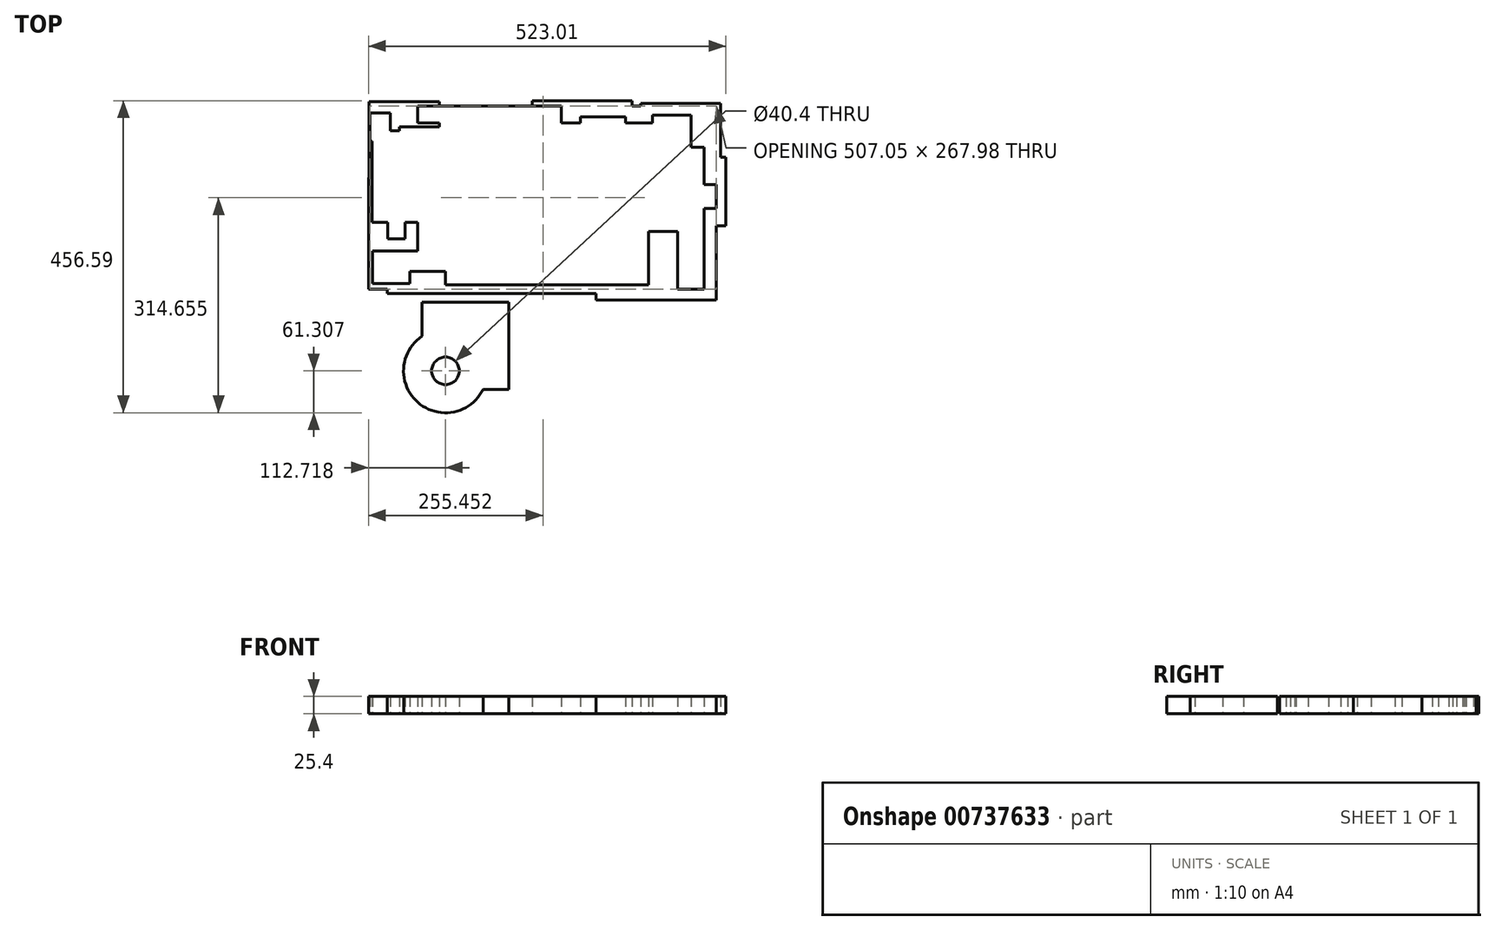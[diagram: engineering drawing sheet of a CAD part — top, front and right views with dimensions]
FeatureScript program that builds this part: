
annotation { "Feature Type Name" : "Feature", "Feature Type Description" : "" }
export const myFeature = defineFeature(function(context is Context, id is Id, definition is map)
    precondition{}
    {
        {
            var Q0;
            Q0=qCreatedBy(makeId("Top.planeOp"),FACE);
            var sketch = newSketch(context, id + "F0", { "sketchPlane" : qUnion([Q0])});
            skLineSegment(sketch, "E0.bottom", {"start": v(-153.8, 86.38) * mm, "end": v(142.89, 86.38) * mm});
            skLineSegment(sketch, "E0.top", {"start": v(-153.8, -120.85) * mm, "end": v(142.89, -120.85) * mm});
            skLineSegment(sketch, "E0.left", {"start": v(-153.8, 86.38) * mm, "end": v(-153.8, -120.85) * mm});
            skLineSegment(sketch, "E0.right", {"start": v(142.89, 86.38) * mm, "end": v(142.89, -120.85) * mm});
            skLineSegment(sketch, "E1.bottom", {"start": v(-264.86, 130.4) * mm, "end": v(-234.77, 130.4) * mm});
            skLineSegment(sketch, "E1.top", {"start": v(-264.86, 89.63) * mm, "end": v(-234.77, 89.63) * mm});
            skLineSegment(sketch, "E1.left", {"start": v(-264.86, 130.4) * mm, "end": v(-264.86, 89.63) * mm});
            skLineSegment(sketch, "E1.right", {"start": v(-234.77, 130.4) * mm, "end": v(-234.77, 89.63) * mm});
            skLineSegment(sketch, "E2.bottom", {"start": v(-229.05, 51.8) * mm, "end": v(-195.45, 51.8) * mm});
            skLineSegment(sketch, "E2.top", {"start": v(-229.05, 13.14) * mm, "end": v(-195.45, 13.14) * mm});
            skLineSegment(sketch, "E2.left", {"start": v(-229.05, 51.8) * mm, "end": v(-229.05, 13.14) * mm});
            skLineSegment(sketch, "E2.right", {"start": v(-195.45, 51.8) * mm, "end": v(-195.45, 13.14) * mm});
            skLineSegment(sketch, "E3.bottom", {"start": v(-238.55, -17.95) * mm, "end": v(-212.9, -17.95) * mm});
            skLineSegment(sketch, "E3.top", {"start": v(-238.55, -53.72) * mm, "end": v(-212.9, -53.72) * mm});
            skLineSegment(sketch, "E3.left", {"start": v(-238.55, -17.95) * mm, "end": v(-238.55, -53.72) * mm});
            skLineSegment(sketch, "E3.right", {"start": v(-212.9, -17.95) * mm, "end": v(-212.9, -53.72) * mm});
            skLineSegment(sketch, "E4.bottom", {"start": v(-261.02, -70.92) * mm, "end": v(-206.29, -70.92) * mm});
            skLineSegment(sketch, "E4.top", {"start": v(-261.02, -118.62) * mm, "end": v(-206.29, -118.62) * mm});
            skLineSegment(sketch, "E4.left", {"start": v(-261.02, -70.92) * mm, "end": v(-261.02, -118.62) * mm});
            skLineSegment(sketch, "E4.right", {"start": v(-206.29, -70.92) * mm, "end": v(-206.29, -118.62) * mm});
            skLineSegment(sketch, "E5.bottom", {"start": v(-194.84, 140.76) * mm, "end": v(224.73, 140.76) * mm});
            skLineSegment(sketch, "E5.top", {"start": v(-194.84, 116.08) * mm, "end": v(224.73, 116.08) * mm});
            skLineSegment(sketch, "E5.left", {"start": v(-194.84, 140.76) * mm, "end": v(-194.84, 116.08) * mm});
            skLineSegment(sketch, "E5.right", {"start": v(224.73, 140.76) * mm, "end": v(224.73, 116.08) * mm});
            skLineSegment(sketch, "E6.bottom", {"start": v(185.58, 80.44) * mm, "end": v(224.07, 80.44) * mm});
            skLineSegment(sketch, "E6.top", {"start": v(185.58, -127.21) * mm, "end": v(224.07, -127.21) * mm});
            skLineSegment(sketch, "E6.left", {"start": v(185.58, 80.44) * mm, "end": v(185.58, -127.21) * mm});
            skLineSegment(sketch, "E6.right", {"start": v(224.07, 80.44) * mm, "end": v(224.07, -127.21) * mm});
            skLineSegment(sketch, "E7.bottom", {"start": v(118.03, 26.13) * mm, "end": v(242.19, 26.13) * mm});
            skLineSegment(sketch, "E7.top", {"start": v(118.03, -8.97) * mm, "end": v(242.19, -8.97) * mm});
            skLineSegment(sketch, "E7.left", {"start": v(118.03, 26.13) * mm, "end": v(118.03, -8.97) * mm});
            skLineSegment(sketch, "E7.right", {"start": v(242.19, 26.13) * mm, "end": v(242.19, -8.97) * mm});
            skLineSegment(sketch, "E8.bottom", {"start": v(-261.46, 140.94) * mm, "end": v(15.43, 140.94) * mm});
            skLineSegment(sketch, "E8.top", {"start": v(-261.46, -29.37) * mm, "end": v(15.43, -29.37) * mm});
            skLineSegment(sketch, "E8.left", {"start": v(-261.46, 140.94) * mm, "end": v(-261.46, -29.37) * mm});
            skLineSegment(sketch, "E8.right", {"start": v(15.43, 140.94) * mm, "end": v(15.43, -29.37) * mm});
            skLineSegment(sketch, "E9.bottom", {"start": v(-194.87, 0) * mm, "end": v(-43.2, 0) * mm});
            skLineSegment(sketch, "E9.top", {"start": v(-194.87, -101.23) * mm, "end": v(-43.2, -101.23) * mm});
            skLineSegment(sketch, "E9.left", {"start": v(-194.87, 0) * mm, "end": v(-194.87, -101.23) * mm});
            skLineSegment(sketch, "E9.right", {"start": v(-43.2, 0) * mm, "end": v(-43.2, -101.23) * mm});
            skLineSegment(sketch, "E10.bottom", {"start": v(-266.79, 36.06) * mm, "end": v(-166.45, 36.06) * mm});
            skLineSegment(sketch, "E10.top", {"start": v(-266.79, -101.23) * mm, "end": v(-166.45, -101.23) * mm});
            skLineSegment(sketch, "E10.left", {"start": v(-266.79, 36.06) * mm, "end": v(-266.79, -101.23) * mm});
            skLineSegment(sketch, "E10.right", {"start": v(-166.45, 36.06) * mm, "end": v(-166.45, -101.23) * mm});
            skLineSegment(sketch, "E11.bottom", {"start": v(-265.99, 147.28) * mm, "end": v(-162.95, 147.28) * mm});
            skLineSegment(sketch, "E11.top", {"start": v(-265.99, -9.08) * mm, "end": v(-162.95, -9.08) * mm});
            skLineSegment(sketch, "E11.left", {"start": v(-265.99, 147.28) * mm, "end": v(-265.99, -9.08) * mm});
            skLineSegment(sketch, "E11.right", {"start": v(-162.95, 147.28) * mm, "end": v(-162.95, -9.08) * mm});
            skLineSegment(sketch, "E12.bottom", {"start": v(-27.01, 148.7) * mm, "end": v(119.24, 148.7) * mm});
            skLineSegment(sketch, "E12.top", {"start": v(-27.01, 69.53) * mm, "end": v(119.24, 69.53) * mm});
            skLineSegment(sketch, "E12.left", {"start": v(-27.01, 148.7) * mm, "end": v(-27.01, 69.53) * mm});
            skLineSegment(sketch, "E12.right", {"start": v(119.24, 148.7) * mm, "end": v(119.24, 69.53) * mm});
            skLineSegment(sketch, "E13.bottom", {"start": v(131.58, 144.51) * mm, "end": v(248.43, 144.51) * mm});
            skLineSegment(sketch, "E13.top", {"start": v(131.58, 48.02) * mm, "end": v(248.43, 48.02) * mm});
            skLineSegment(sketch, "E13.left", {"start": v(131.58, 144.51) * mm, "end": v(131.58, 48.02) * mm});
            skLineSegment(sketch, "E13.right", {"start": v(248.43, 144.51) * mm, "end": v(248.43, 48.02) * mm});
            skLineSegment(sketch, "E14.bottom", {"start": v(161.48, 65.64) * mm, "end": v(256.22, 65.64) * mm});
            skLineSegment(sketch, "E14.top", {"start": v(161.48, -34.64) * mm, "end": v(256.22, -34.64) * mm});
            skLineSegment(sketch, "E14.left", {"start": v(161.48, 65.64) * mm, "end": v(161.48, -34.64) * mm});
            skLineSegment(sketch, "E14.right", {"start": v(256.22, 65.64) * mm, "end": v(256.22, -34.64) * mm});
            skLineSegment(sketch, "E15.bottom", {"start": v(86.74, 43.89) * mm, "end": v(191.53, 43.89) * mm});
            skLineSegment(sketch, "E15.top", {"start": v(86.74, -42.94) * mm, "end": v(191.53, -42.94) * mm});
            skLineSegment(sketch, "E15.left", {"start": v(86.74, 43.89) * mm, "end": v(86.74, -42.94) * mm});
            skLineSegment(sketch, "E15.right", {"start": v(191.53, 43.89) * mm, "end": v(191.53, -42.94) * mm});
            skLineSegment(sketch, "E16.bottom", {"start": v(66.53, -17.95) * mm, "end": v(241.99, -17.95) * mm});
            skLineSegment(sketch, "E16.top", {"start": v(66.53, -142.8) * mm, "end": v(241.99, -142.8) * mm});
            skLineSegment(sketch, "E16.left", {"start": v(66.53, -17.95) * mm, "end": v(66.53, -142.8) * mm});
            skLineSegment(sketch, "E16.right", {"start": v(241.99, -17.95) * mm, "end": v(241.99, -142.8) * mm});
            skLineSegment(sketch, "E17.bottom", {"start": v(-239.16, -101.23) * mm, "end": v(116.8, -101.23) * mm});
            skLineSegment(sketch, "E17.top", {"start": v(-239.16, -133.38) * mm, "end": v(116.8, -133.38) * mm});
            skLineSegment(sketch, "E17.left", {"start": v(-239.16, -101.23) * mm, "end": v(-239.16, -133.38) * mm});
            skLineSegment(sketch, "E17.right", {"start": v(116.8, -101.23) * mm, "end": v(116.8, -133.38) * mm});
            skLineSegment(sketch, "E18.bottom", {"start": v(-266.79, -70.92) * mm, "end": v(-194.87, -70.92) * mm});
            skLineSegment(sketch, "E18.top", {"start": v(-266.79, -127.21) * mm, "end": v(-194.87, -127.21) * mm});
            skLineSegment(sketch, "E18.left", {"start": v(-266.79, -70.92) * mm, "end": v(-266.79, -127.21) * mm});
            skLineSegment(sketch, "E18.right", {"start": v(-194.87, -70.92) * mm, "end": v(-194.87, -127.21) * mm});
            skLineSegment(sketch, "E19.bottom", {"start": v(-94.17, 47.4) * mm, "end": v(94.18, 47.4) * mm});
            skLineSegment(sketch, "E19.top", {"start": v(-94.17, -60.92) * mm, "end": v(94.18, -60.92) * mm});
            skLineSegment(sketch, "E19.left", {"start": v(-94.17, 47.4) * mm, "end": v(-94.17, -60.92) * mm});
            skLineSegment(sketch, "E19.right", {"start": v(94.18, 47.4) * mm, "end": v(94.18, -60.92) * mm});
            skLineSegment(sketch, "E20.bottom", {"start": v(-17.53, 13.14) * mm, "end": v(15.43, 13.14) * mm});
            skLineSegment(sketch, "E20.top", {"start": v(-17.53, -17.95) * mm, "end": v(15.43, -17.95) * mm});
            skLineSegment(sketch, "E20.left", {"start": v(-17.53, 13.14) * mm, "end": v(-17.53, -17.95) * mm});
            skLineSegment(sketch, "E20.right", {"start": v(15.43, 13.14) * mm, "end": v(15.43, -17.95) * mm});
            skLineSegment(sketch, "E21.bottom", {"start": v(-122.33, 65.96) * mm, "end": v(0, 65.96) * mm});
            skLineSegment(sketch, "E21.top", {"start": v(-122.33, 0) * mm, "end": v(0, 0) * mm});
            skLineSegment(sketch, "E21.left", {"start": v(-122.33, 65.96) * mm, "end": v(-122.33, 0) * mm});
            skLineSegment(sketch, "E21.right", {"start": v(0, 65.96) * mm, "end": v(0, 0) * mm});
            skLineSegment(sketch, "E22.bottom", {"start": v(36.74, 51.8) * mm, "end": v(118.03, 51.8) * mm});
            skLineSegment(sketch, "E22.top", {"start": v(36.74, -6.76) * mm, "end": v(118.03, -6.76) * mm});
            skLineSegment(sketch, "E22.left", {"start": v(36.74, 51.8) * mm, "end": v(36.74, -6.76) * mm});
            skLineSegment(sketch, "E22.right", {"start": v(118.03, 51.8) * mm, "end": v(118.03, -6.76) * mm});
            skLineSegment(sketch, "E23.bottom", {"start": v(-111.93, -55.78) * mm, "end": v(85.5, -55.78) * mm});
            skLineSegment(sketch, "E23.top", {"start": v(-111.93, -88.15) * mm, "end": v(85.5, -88.15) * mm});
            skLineSegment(sketch, "E23.left", {"start": v(-111.93, -55.78) * mm, "end": v(-111.93, -88.15) * mm});
            skLineSegment(sketch, "E23.right", {"start": v(85.5, -55.78) * mm, "end": v(85.5, -88.15) * mm});
            skLineSegment(sketch, "E24.bottom", {"start": v(-138.47, 68.65) * mm, "end": v(-68.07, 68.65) * mm});
            skLineSegment(sketch, "E24.top", {"start": v(-138.47, -84.1) * mm, "end": v(-68.07, -84.1) * mm});
            skLineSegment(sketch, "E24.left", {"start": v(-138.47, 68.65) * mm, "end": v(-138.47, -84.1) * mm});
            skLineSegment(sketch, "E24.right", {"start": v(-68.07, 68.65) * mm, "end": v(-68.07, -84.1) * mm});
            skLineSegment(sketch, "E25.bottom", {"start": v(-132.89, 135.4) * mm, "end": v(-35.57, 135.4) * mm});
            skLineSegment(sketch, "E25.top", {"start": v(-132.89, 58.1) * mm, "end": v(-35.57, 58.1) * mm});
            skLineSegment(sketch, "E25.left", {"start": v(-132.89, 135.4) * mm, "end": v(-132.89, 58.1) * mm});
            skLineSegment(sketch, "E25.right", {"start": v(-35.57, 135.4) * mm, "end": v(-35.57, 58.1) * mm});
            skLineSegment(sketch, "E26.bottom", {"start": v(43.46, 124.93) * mm, "end": v(109.64, 124.93) * mm});
            skLineSegment(sketch, "E26.top", {"start": v(43.46, 21.95) * mm, "end": v(109.64, 21.95) * mm});
            skLineSegment(sketch, "E26.left", {"start": v(43.46, 124.93) * mm, "end": v(43.46, 21.95) * mm});
            skLineSegment(sketch, "E26.right", {"start": v(109.64, 124.93) * mm, "end": v(109.64, 21.95) * mm});
            skLineSegment(sketch, "E27.bottom", {"start": v(-221.56, 110.52) * mm, "end": v(-95.15, 110.52) * mm});
            skLineSegment(sketch, "E27.top", {"start": v(-221.56, 75.8) * mm, "end": v(-95.15, 75.8) * mm});
            skLineSegment(sketch, "E27.left", {"start": v(-221.56, 110.52) * mm, "end": v(-221.56, 75.8) * mm});
            skLineSegment(sketch, "E27.right", {"start": v(-95.15, 110.52) * mm, "end": v(-95.15, 75.8) * mm});
            skLineSegment(sketch, "E28.bottom", {"start": v(148.68, 127.62) * mm, "end": v(205.26, 127.62) * mm});
            skLineSegment(sketch, "E28.top", {"start": v(148.68, 59.04) * mm, "end": v(205.26, 59.04) * mm});
            skLineSegment(sketch, "E28.left", {"start": v(148.68, 127.62) * mm, "end": v(148.68, 59.04) * mm});
            skLineSegment(sketch, "E28.right", {"start": v(205.26, 127.62) * mm, "end": v(205.26, 59.04) * mm});
            skLineSegment(sketch, "E29.bottom", {"start": v(-244.9, 104.56) * mm, "end": v(-179.19, 104.56) * mm});
            skLineSegment(sketch, "E29.top", {"start": v(-244.9, 8.68) * mm, "end": v(-179.19, 8.68) * mm});
            skLineSegment(sketch, "E29.left", {"start": v(-244.9, 104.56) * mm, "end": v(-244.9, 8.68) * mm});
            skLineSegment(sketch, "E29.right", {"start": v(-179.19, 104.56) * mm, "end": v(-179.19, 8.68) * mm});
            skLineSegment(sketch, "E30.bottom", {"start": v(-188.57, -273.5) * mm, "end": v(-61.27, -273.5) * mm});
            skLineSegment(sketch, "E30.top", {"start": v(-188.57, -146.19) * mm, "end": v(-61.27, -146.19) * mm});
            skLineSegment(sketch, "E30.left", {"start": v(-188.57, -273.5) * mm, "end": v(-188.57, -146.19) * mm});
            skLineSegment(sketch, "E30.right", {"start": v(-61.27, -273.5) * mm, "end": v(-61.27, -146.19) * mm});
            skCircle(sketch, "E31", {"center": v(-154.07, -246.57) * mm, "radius": 61.3 * mm});
            skCircle(sketch, "E32", {"center": v(-154.07, -246.57) * mm, "radius": 20.2 * mm});
            skSolve(sketch);
        }
        {
            var Q0;
            Q0 = qSketchRegion(id + "F0", true);
            extrude(context, id + "F1", {"entities" : qUnion([Q0]), "depth" : 25.4 * mm, "offsetDistance" : 25.4 * mm});
        }
    });
